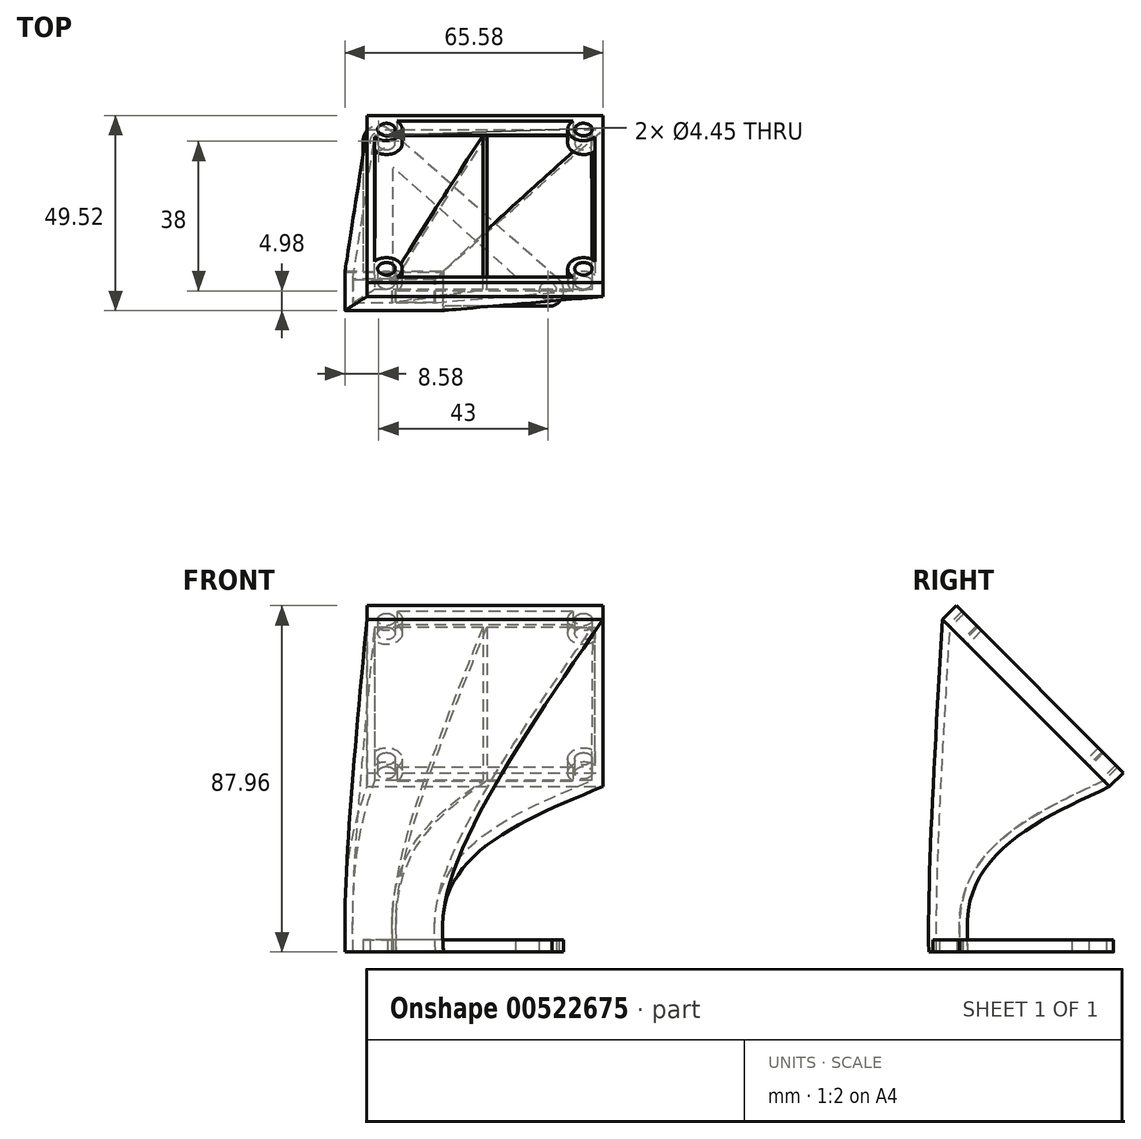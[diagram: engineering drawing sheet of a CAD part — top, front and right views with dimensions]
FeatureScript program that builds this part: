
annotation { "Feature Type Name" : "Feature", "Feature Type Description" : "" }
export const myFeature = defineFeature(function(context is Context, id is Id, definition is map)
    precondition{}
    {
        {
            var Q0;
            Q0=qCreatedBy(makeId("Top.planeOp"),FACE);
            var sketch = newSketch(context, id + "F0", { "sketchPlane" : qUnion([Q0])});
            skCircle(sketch, "E0", {"center": v(-13, 0) * mm, "radius": 2.25 * mm});
            skCircle(sketch, "E1", {"center": v(-56, 38) * mm, "radius": 2.25 * mm});
            skSolve(sketch);
        }
        {
            var Q0;
            Q0=qCreatedBy(makeId("Top.planeOp"),FACE);
            var sketch = newSketch(context, id + "F1", { "sketchPlane" : qUnion([Q0])});
            skLineSegment(sketch, "E2.left", {"start": v(-64.54, 5.04) * mm, "end": v(-64.54, -4.96) * mm});
            skLineSegment(sketch, "E2.right", {"start": v(-39.54, 5.04) * mm, "end": v(-39.54, -4.96) * mm});
            skLineSegment(sketch, "E3.left", {"start": v(-51.54, -4.71) * mm, "end": v(-51.54, 4.79) * mm});
            skLineSegment(sketch, "E3.right", {"start": v(-52.54, -4.71) * mm, "end": v(-52.54, 4.79) * mm});
            skPoint(sketch, "E3.middle", {"position": v(-52.04, 5.04) * mm});
            skPoint(sketch, "E3.bottom.end.orphan", {"position": v(-52.54, -15.21) * mm});
            skPoint(sketch, "E3.bottom.start.orphan", {"position": v(-51.54, -15.21) * mm});
            skPoint(sketch, "E3.top.end.orphan", {"position": v(-52.54, 25.3) * mm});
            skPoint(sketch, "E3.top.start.orphan", {"position": v(-51.54, 25.3) * mm});
            skLineSegment(sketch, "E4", {"start": v(-52.54, 4.79) * mm, "end": v(-51.54, 4.79) * mm});
            skLineSegment(sketch, "E5", {"start": v(-64.54, 5.04) * mm, "end": v(-39.54, 5.04) * mm});
            skLineSegment(sketch, "E6", {"start": v(-52.54, -4.71) * mm, "end": v(-51.54, -4.71) * mm});
            skLineSegment(sketch, "E7", {"start": v(-39.54, -4.96) * mm, "end": v(-64.54, -4.96) * mm});
            skSolve(sketch);
        }
        {
            var Q0;
            Q0=makeQuery(id+"F1.imprint","IMPRINT",FACE,{"disambiguationData":[TD([[makeQuery(id+"F1.imprint","IMPRINT",EDGE,{"derivedFrom":sQuery(id+"F1.wireOp",EDGE,"E2.left")}),1.0]])]});
            var sketch = newSketch(context, id + "F2", { "sketchPlane" : qUnion([Q0])});
            skLineSegment(sketch, "E8.0", {"start": v(-64.54, 5.04) * mm, "end": v(-39.54, 5.04) * mm});
            skLineSegment(sketch, "E9.0", {"start": v(-39.54, 5.04) * mm, "end": v(-39.54, -4.96) * mm});
            skLineSegment(sketch, "E10.0", {"start": v(-39.54, -4.96) * mm, "end": v(-64.54, -4.96) * mm});
            skLineSegment(sketch, "E11.0", {"start": v(-64.54, 5.04) * mm, "end": v(-64.54, -4.96) * mm});
            skSolve(sketch);
        }
        {
            var Q0;
            Q0=qCreatedBy(makeId("Top.planeOp"),FACE);
            cPlane(context, id + "F3", {"entities" : qUnion([Q0]), "cplaneType" : CPlaneType.OFFSET, "offset" : 42 * mm, "width" : 150 * mm, "height" : 150 * mm});
        }
        {
            var Q0;
            Q0=qCreatedBy(makeId("Front.planeOp"),FACE);
            cPlane(context, id + "F4", {"entities" : qUnion([Q0]), "cplaneType" : CPlaneType.OFFSET, "offset" : 41 * mm, "oppositeDirection" : true, "width" : 150 * mm, "height" : 150 * mm});
        }
        {
            var Q0;
            Q0=qCreatedBy(id+"F3.planeOp",FACE);
            var sketch = newSketch(context, id + "F5", { "sketchPlane" : qUnion([Q0])});
            skLineSegment(sketch, "E12", {"start": v(-69.45, 41) * mm, "end": v(5.55, 41) * mm});
            skSolve(sketch);
        }
        {
            var Q0;
            Q0=sQuery(id+"F5.wireOp",EDGE,"E12");
            cPlane(context, id + "F6", {"entities" : qUnion([Q0]), "cplaneType" : CPlaneType.LINE_ANGLE, "offset" : 25 * mm, "angle" : 45 * degree, "width" : 150 * mm, "height" : 150 * mm});
        }
        {
            var Q0;
            Q0=qCreatedBy(id+"F6.planeOp",FACE);
            var sketch = newSketch(context, id + "F7", { "sketchPlane" : qUnion([Q0])});
            skLineSegment(sketch, "E13.top", {"start": v(59, 60.7) * mm, "end": v(-1, 60.7) * mm});
            skLineSegment(sketch, "E13.left", {"start": v(59, 0.7) * mm, "end": v(59, 60.7) * mm});
            skLineSegment(sketch, "E13.right", {"start": v(-1, 0.7) * mm, "end": v(-1, 60.7) * mm});
            skPoint(sketch, "E14.orphan", {"position": v(69.45, 0.7) * mm});
            skPoint(sketch, "E15.0.end.orphan", {"position": v(-5.55, 0.7) * mm});
            skLineSegment(sketch, "E16", {"start": v(59, 0.7) * mm, "end": v(-1, 0.7) * mm});
            skLineSegment(sketch, "E17.left", {"start": v(28.5, 60.46) * mm, "end": v(28.5, 0.96) * mm});
            skLineSegment(sketch, "E17.right", {"start": v(29.5, 60.46) * mm, "end": v(29.5, 0.96) * mm});
            skLineSegment(sketch, "E18", {"start": v(29.5, 60.46) * mm, "end": v(28.5, 60.46) * mm});
            skLineSegment(sketch, "E19", {"start": v(29.5, 0.96) * mm, "end": v(28.5, 0.96) * mm});
            skSolve(sketch);
        }
        {
            var Q0;
            Q0=makeQuery(id+"F7.imprint","IMPRINT",FACE,{"disambiguationData":[TD([[makeQuery(id+"F7.imprint","IMPRINT",EDGE,{"derivedFrom":sQuery(id+"F7.wireOp",EDGE,"E13.top")}),1.0]])]});
            var sketch = newSketch(context, id + "F8", { "sketchPlane" : qUnion([Q0])});
            skLineSegment(sketch, "E20.0", {"start": v(59, 0.7) * mm, "end": v(-1, 0.7) * mm});
            skLineSegment(sketch, "E21.0", {"start": v(59, 0.7) * mm, "end": v(59, 60.7) * mm});
            skLineSegment(sketch, "E22.0", {"start": v(59, 60.7) * mm, "end": v(-1, 60.7) * mm});
            skLineSegment(sketch, "E23.0", {"start": v(-1, 0.7) * mm, "end": v(-1, 60.7) * mm});
            skSolve(sketch);
        }
        {
            var Q0;
            Q0=qCreatedBy(makeId("Top.planeOp"),FACE);
            cPlane(context, id + "F9", {"entities" : qUnion([Q0]), "cplaneType" : CPlaneType.OFFSET, "offset" : 10 * mm, "width" : 150 * mm, "height" : 150 * mm});
        }
        {
            var Q0;
            Q0=qCreatedBy(id+"F9.planeOp",FACE);
            var sketch = newSketch(context, id + "F10", { "sketchPlane" : qUnion([Q0])});
            skLineSegment(sketch, "E24.left", {"start": v(-51.54, -4.71) * mm, "end": v(-51.54, 4.79) * mm});
            skLineSegment(sketch, "E24.right", {"start": v(-52.54, -4.71) * mm, "end": v(-52.54, 4.79) * mm});
            skLineSegment(sketch, "E25", {"start": v(-52.54, -4.71) * mm, "end": v(-51.54, -4.71) * mm});
            skLineSegment(sketch, "E26", {"start": v(-52.54, 4.79) * mm, "end": v(-51.54, 4.79) * mm});
            skLineSegment(sketch, "E27", {"start": v(-39.54, 5.04) * mm, "end": v(-39.54, -4.96) * mm});
            skLineSegment(sketch, "E28", {"start": v(-64.54, 5.04) * mm, "end": v(-64.54, -4.96) * mm});
            skLineSegment(sketch, "E29", {"start": v(-64.54, -4.96) * mm, "end": v(-39.54, -4.96) * mm});
            skLineSegment(sketch, "E30", {"start": v(-64.54, 5.04) * mm, "end": v(-39.54, 5.04) * mm});
            skSolve(sketch);
        }
        {
            var Q0;
            Q0=makeQuery(id+"F10.imprint","IMPRINT",FACE,{"disambiguationData":[TD([[makeQuery(id+"F10.imprint","IMPRINT",EDGE,{"derivedFrom":sQuery(id+"F10.wireOp",EDGE,"E24.left")}),-1.0]])]});
            var sketch = newSketch(context, id + "F11", { "sketchPlane" : qUnion([Q0])});
            skLineSegment(sketch, "E31.0", {"start": v(-64.54, 5.04) * mm, "end": v(-39.54, 5.04) * mm});
            skLineSegment(sketch, "E32.0", {"start": v(-39.54, 5.04) * mm, "end": v(-39.54, -4.96) * mm});
            skLineSegment(sketch, "E33.0", {"start": v(-64.54, 5.04) * mm, "end": v(-64.54, -4.96) * mm});
            skLineSegment(sketch, "E34.0", {"start": v(-64.54, -4.96) * mm, "end": v(-39.54, -4.96) * mm});
            skSolve(sketch);
        }
        {
            var Q0;
            Q0=qSketchRegion(id+"F2",true);
            var Q1;
            Q1=qSketchRegion(id+"F11",true);
            var Q2;
            Q2=qSketchRegion(id+"F8",true);
            loft(context, id + "F12", {"sheetProfilesArray" : [{ "sheetProfileEntities" : qUnion([Q0]) }, { "sheetProfileEntities" : qUnion([Q1]) }, { "sheetProfileEntities" : qUnion([Q2]) }]});
        }
        {
            var Q0;
            Q0=makeQuery(id+"F12.opLoft","CAP_FACE",FACE,{"disambiguationData":[OSD([makeQuery(id+"F8.imprint","IMPRINT",FACE,{"disambiguationData":[TD([[makeQuery(id+"F8.imprint","IMPRINT",EDGE,{"derivedFrom":makeQuery(id+"F7.imprint","IMPRINT",EDGE,{"derivedFrom":sQuery(id+"F7.wireOp",EDGE,"E17.left")})}),1.0]])]})])],"isStart":true});
            var Q1;
            Q1=makeQuery(id+"F12.opLoft","CAP_FACE",FACE,{"disambiguationData":[OSD([makeQuery(id+"F2.imprint","IMPRINT",FACE,{"disambiguationData":[TD([[makeQuery(id+"F2.imprint","IMPRINT",EDGE,{"derivedFrom":makeQuery(id+"F1.imprint","IMPRINT",EDGE,{"derivedFrom":sQuery(id+"F1.wireOp",EDGE,"E3.left")})}),1.0]])]})])],"isStart":true});
            var Q2;
            Q2=makeQuery(id+"F12.opLoft","SWEPT_BODY",BODY,{"disambiguationData":[OSD([makeQuery(id+"F1.imprint","IMPRINT",FACE,{"disambiguationData":[TD([[makeQuery(id+"F1.imprint","IMPRINT",EDGE,{"derivedFrom":sQuery(id+"F1.wireOp",EDGE,"E2.bottom")}),-1.0]])]}),makeQuery(id+"F7.imprint","IMPRINT",FACE,{"disambiguationData":[TD([[makeQuery(id+"F7.imprint","IMPRINT",EDGE,{"derivedFrom":sQuery(id+"F7.wireOp",EDGE,"E13.top")}),1.0]])]}),sQuery(id+"F10.wireOp",EDGE,"53b9d818-3cec-4563-ae3e-a3bfcee2ebea.0")])]});
            shell(context, id + "F13", {"entities" : qUnion([Q0, Q1]), "parts" : qUnion([Q2]), "thickness" : 2 * mm});
        }
        {
            var Q1;
            Q1=makeQuery(id+"F1.imprint","IMPRINT",FACE,{"disambiguationData":[TD([[makeQuery(id+"F1.imprint","IMPRINT",EDGE,{"derivedFrom":sQuery(id+"F1.wireOp",EDGE,"E3.left")}),1.0]])]});
            var Q2;
            Q2=makeQuery(id+"F10.imprint","IMPRINT",FACE,{"disambiguationData":[TD([[makeQuery(id+"F10.imprint","IMPRINT",EDGE,{"derivedFrom":sQuery(id+"F10.wireOp",EDGE,"E24.left")}),1.0]])]});
            var Q3;
            Q3=makeQuery(id+"F7.imprint","IMPRINT",FACE,{"disambiguationData":[TD([[makeQuery(id+"F7.imprint","IMPRINT",EDGE,{"derivedFrom":sQuery(id+"F7.wireOp",EDGE,"E17.left")}),1.0]])]});
            loft(context, id + "F14", {"operationType" : NewBodyOperationType.ADD, "sheetProfilesArray" : [{ "sheetProfileEntities" : qUnion([Q1]) }, { "sheetProfileEntities" : qUnion([Q2]) }, { "sheetProfileEntities" : qUnion([Q3]) }]});
        }
        {
            var Q0;
            Q0=qCreatedBy(id+"F6.planeOp",FACE);
            var sketch = newSketch(context, id + "F15", { "sketchPlane" : qUnion([Q0])});
            skLineSegment(sketch, "E35.0", {"start": v(59, 60.7) * mm, "end": v(59, 0.7) * mm});
            skLineSegment(sketch, "E36.0", {"start": v(59, 0.7) * mm, "end": v(-1, 0.7) * mm});
            skLineSegment(sketch, "E37.0", {"start": v(-1, 0.7) * mm, "end": v(-1, 60.7) * mm});
            skLineSegment(sketch, "E38.0", {"start": v(29.5, 60.7) * mm, "end": v(59, 60.7) * mm});
            skLineSegment(sketch, "E39.0", {"start": v(-1, 60.7) * mm, "end": v(29.5, 60.7) * mm});
            skCircle(sketch, "E40", {"center": v(54.03, 5.68) * mm, "radius": 2.23 * mm});
            skCircle(sketch, "E41", {"center": v(3.98, 5.68) * mm, "radius": 2.23 * mm});
            skCircle(sketch, "E42", {"center": v(3.97, 55.73) * mm, "radius": 2.23 * mm});
            skCircle(sketch, "E43", {"center": v(54.02, 55.73) * mm, "radius": 2.23 * mm});
            skArc(sketch, "E44", {"start": v(51.35, 58.7) * mm, "mid": v(51.2, 52.9) * mm, "end": v(57, 53.06) * mm});
            skArc(sketch, "E45", {"start": v(57, 8.36) * mm, "mid": v(51.2, 8.51) * mm, "end": v(51.35, 2.7) * mm});
            skArc(sketch, "E46", {"start": v(1, 53.06) * mm, "mid": v(6.8, 52.9) * mm, "end": v(6.65, 58.7) * mm});
            skLineSegment(sketch, "E47.0", {"start": v(57, 53.06) * mm, "end": v(57, 8.36) * mm});
            skLineSegment(sketch, "E48.trimOffspring", {"start": v(51.35, 2.7) * mm, "end": v(6.65, 2.7) * mm});
            skLineSegment(sketch, "E49.trimOffspring", {"start": v(1, 8.36) * mm, "end": v(1, 53.06) * mm});
            skArc(sketch, "E50.trimOffspring", {"start": v(6.65, 2.7) * mm, "mid": v(6.8, 8.51) * mm, "end": v(1, 8.36) * mm});
            skLineSegment(sketch, "E51.trimOffspring", {"start": v(6.65, 58.7) * mm, "end": v(51.35, 58.7) * mm});
            skPoint(sketch, "E52.orphan", {"position": v(28.5, 60.7) * mm});
            skSolve(sketch);
        }
        {
            var Q0;
            Q0=makeQuery(id+"F15.imprint","IMPRINT",FACE,{"disambiguationData":[TD([[makeQuery(id+"F15.imprint","IMPRINT",EDGE,{"derivedFrom":sQuery(id+"F15.wireOp",EDGE,"E35.0")}),-1.0]])]});
            extrude(context, id + "F16", {"entities" : qUnion([Q0]), "operationType" : NewBodyOperationType.ADD, "depth" : 5 * mm, "offsetDistance" : 25 * mm});
        }
        {
            var Q0;
            Q0=qCreatedBy(makeId("Top.planeOp"),FACE);
            var sketch = newSketch(context, id + "F17", { "sketchPlane" : qUnion([Q0])});
            skPoint(sketch, "E53.0", {"position": v(-56, 38) * mm});
            skPoint(sketch, "E54.0", {"position": v(-13, 0) * mm});
            skPoint(sketch, "E55.0", {"position": v(0, 0) * mm});
            skArc(sketch, "E56", {"start": v(-11.96, -3.86) * mm, "mid": v(-9.13, -1.02) * mm, "end": v(-10.2, 2.85) * mm});
            skArc(sketch, "E57", {"start": v(-53.35, 41) * mm, "mid": v(-57.64, 41.65) * mm, "end": v(-60, 38) * mm});
            skLineSegment(sketch, "E58", {"start": v(-10.2, 2.85) * mm, "end": v(-53.35, 41) * mm});
            skLineSegment(sketch, "E59", {"start": v(-60, 38) * mm, "end": v(-60, 5.04) * mm});
            skLineSegment(sketch, "E60", {"start": v(-21.18, 3.7) * mm, "end": v(-52.3, 31.42) * mm});
            skPoint(sketch, "E61.orphan", {"position": v(-51.54, 5.04) * mm});
            skCircle(sketch, "E62", {"center": v(-56, 38) * mm, "radius": 2.23 * mm});
            skCircle(sketch, "E63", {"center": v(-13, 0) * mm, "radius": 2.23 * mm});
            skLineSegment(sketch, "E64", {"start": v(-11.96, -3.86) * mm, "end": v(-40.68, -3.86) * mm});
            skLineSegment(sketch, "E65", {"start": v(-40.68, -3.86) * mm, "end": v(-40.68, 3.74) * mm});
            skLineSegment(sketch, "E66", {"start": v(-40.68, 3.74) * mm, "end": v(-60, 3.74) * mm});
            skLineSegment(sketch, "E67", {"start": v(-60, 3.74) * mm, "end": v(-60, 5.04) * mm});
            skLineSegment(sketch, "E68", {"start": v(-52.3, 4.46) * mm, "end": v(-52.3, 31.42) * mm});
            skLineSegment(sketch, "E69", {"start": v(-21.18, 3.7) * mm, "end": v(-40.01, 3.5) * mm});
            skLineSegment(sketch, "E70", {"start": v(-40.01, 3.5) * mm, "end": v(-40.02, 4.46) * mm});
            skLineSegment(sketch, "E71", {"start": v(-40.02, 4.46) * mm, "end": v(-52.3, 4.46) * mm});
            skSolve(sketch);
        }
        {
            var Q0;
            Q0=makeQuery(id+"F17.imprint","IMPRINT",FACE,{"disambiguationData":[TD([[makeQuery(id+"F17.imprint","IMPRINT",EDGE,{"derivedFrom":sQuery(id+"F17.wireOp",EDGE,"E56")}),1.0]])]});
            var Q1;
            Q1=makeQuery(id+"F12.opLoft","SWEPT_FACE",FACE,{"disambiguationData":[OSD([sQuery(id+"F7.wireOp",EDGE,"E13.left"),sQuery(id+"F7.wireOp",EDGE,"E16"),sQuery(id+"F7.wireOp",EDGE,"E17.right"),sQuery(id+"F10.wireOp",EDGE,"07188e4b-1e0c-4a04-9c08-0290d4258171.0"),sQuery(id+"F10.wireOp",EDGE,"53b9d818-3cec-4563-ae3e-a3bfcee2ebea.0"),sQuery(id+"F10.wireOp",EDGE,"E24.right")])]});
            extrude(context, id + "F18", {"entities" : qUnion([Q0]), "operationType" : NewBodyOperationType.ADD, "depth" : 3 * mm, "endBoundEntityFace" : qUnion([Q1]), "offsetDistance" : 25 * mm});
        }
    });
